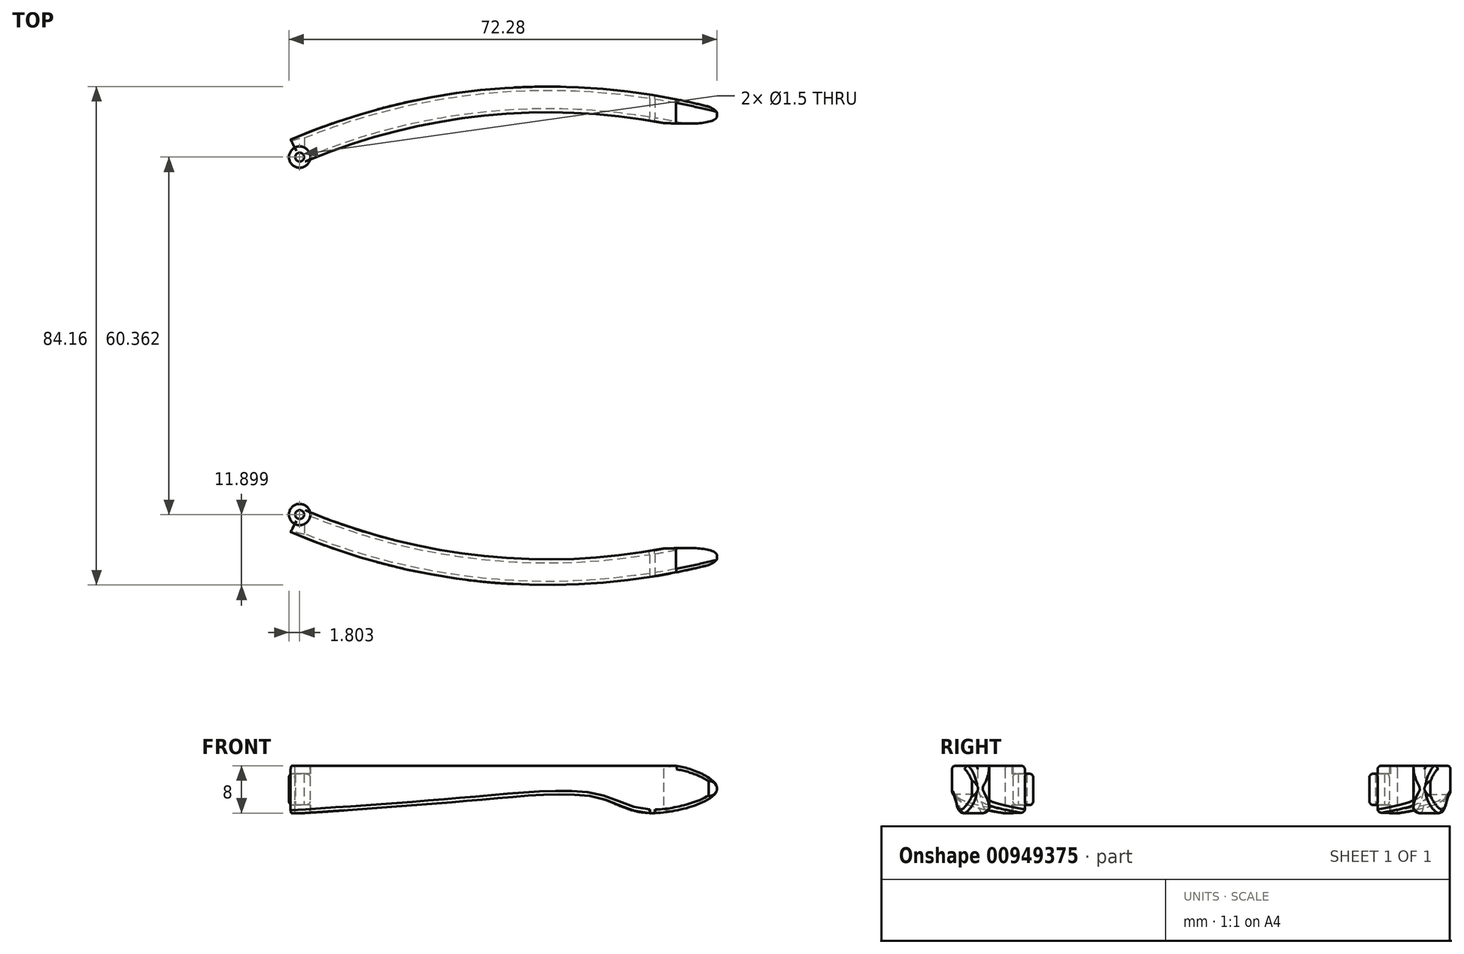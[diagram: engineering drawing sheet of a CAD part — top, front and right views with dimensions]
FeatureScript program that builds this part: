
annotation { "Feature Type Name" : "Feature", "Feature Type Description" : "" }
export const myFeature = defineFeature(function(context is Context, id is Id, definition is map)
    precondition{}
    {
        {
            var Q0;
            Q0=qCreatedBy(makeId("Top.planeOp"),FACE);
            var sketch = newSketch(context, id + "F0", { "sketchPlane" : qUnion([Q0])});
            skArc(sketch, "E0.0", {"start": v(25.58, 38.7) * mm, "mid": v(-10.17, 41.73) * mm, "end": v(-45, 33.11) * mm});
            skFitSpline(sketch, "E1", {"points": [v(25.58, 38.7) * mm, v(26.65, 36.57) * mm, v(17.96, 35.93) * mm], "startDerivative": vector(14.5, -5.54) * mm, "endDerivative": vector(-9.45, 0.25) * mm});
            skArc(sketch, "E2", {"start": v(17.96, 35.93) * mm, "mid": v(-13.01, 37.1) * mm, "end": v(-43, 29.25) * mm});
            skCircle(sketch, "E3", {"center": v(-43.48, 30.18) * mm, "radius": 0.75 * mm});
            skLineSegment(sketch, "E4", {"start": v(-45, 33.11) * mm, "end": v(-44.3, 31.78) * mm});
            skCircle(sketch, "E5.0", {"center": v(-43.48, 30.18) * mm, "radius": 1.8 * mm});
            skLineSegment(sketch, "E6", {"start": v(-44.3, 31.78) * mm, "end": v(-43, 29.25) * mm});
            skPoint(sketch, "E7", {"position": v(27, 36.94) * mm});
            skLineSegment(sketch, "E8", {"start": v(9.91, 0) * mm, "end": v(-97.59, 0) * mm, "construction": true});
            skLineSegment(sketch, "E9.MirrorCS", {"start": v(-45, -33.11) * mm, "end": v(-44.3, -31.78) * mm});
            skLineSegment(sketch, "E10.MirrorCS", {"start": v(-44.3, -31.78) * mm, "end": v(-43, -29.25) * mm});
            skCircle(sketch, "E11.MirrorC", {"center": v(-43.48, -30.18) * mm, "radius": 0.75 * mm});
            skFitSpline(sketch, "E12.MirrorCS", {"points": [v(25.58, -38.7) * mm, v(26.65, -36.57) * mm, v(17.96, -35.93) * mm], "startDerivative": vector(14.5, 5.54) * mm, "endDerivative": vector(-9.45, -0.25) * mm});
            skPoint(sketch, "E13.MirrorP", {"position": v(27, -36.94) * mm});
            skArc(sketch, "E14.MirrorCS", {"start": v(25.58, -38.7) * mm, "mid": v(-10.17, -41.73) * mm, "end": v(-45, -33.11) * mm});
            skCircle(sketch, "E15.MirrorC", {"center": v(-43.48, -30.18) * mm, "radius": 1.8 * mm});
            skArc(sketch, "E16.MirrorCS", {"start": v(17.96, -35.93) * mm, "mid": v(-13.01, -37.1) * mm, "end": v(-43, -29.25) * mm});
            skLineSegment(sketch, "E17", {"start": v(-45.08, 29.35) * mm, "end": v(-48.74, 36.44) * mm, "construction": true});
            skSolve(sketch);
        }
        {
            var Q0;
            Q0=makeQuery(id+"F0.imprint","IMPRINT",FACE,{"disambiguationData":[TD([[makeQuery(id+"F0.imprint","IMPRINT",EDGE,{"derivedFrom":sQuery(id+"F0.wireOp",EDGE,"E0.0")}),1.0]])]});
            var Q1;
            {var subQ2=sQuery(id+"F0.wireOp",EDGE,"E9.MirrorCS");Q1=makeQuery(id+"F0.imprint","IMPRINT",FACE,{"disambiguationData":[TD([[makeQuery(id+"F0.imprint","IMPRINT",EDGE,{"derivedFrom":subQ2}),-1.0]])]});}
            extrude(context, id + "F1", {"entities" : qUnion([Q0, Q1]), "endBound" : BoundingType.SYMMETRIC, "depth" : 8 * mm, "offsetDistance" : 25 * mm});
        }
        {
            var Q0;
            {var subQ1=sQuery(id+"F0.wireOp",EDGE,"E3");Q0=makeQuery(id+"F0.imprint","IMPRINT",FACE,{"disambiguationData":[TD([[makeQuery(id+"F0.imprint","IMPRINT",EDGE,{"derivedFrom":subQ1}),-1.0]])]});}
            var Q1;
            {var subQ0=sQuery(id+"F0.wireOp",EDGE,"E6");Q1=makeQuery(id+"F0.imprint","IMPRINT",FACE,{"disambiguationData":[TD([[makeQuery(id+"F0.imprint","IMPRINT",EDGE,{"derivedFrom":subQ0}),1.0]])]});}
            var Q2;
            {var subQ0=sQuery(id+"F0.wireOp",EDGE,"E10.MirrorCS");Q2=makeQuery(id+"F0.imprint","IMPRINT",FACE,{"disambiguationData":[TD([[makeQuery(id+"F0.imprint","IMPRINT",EDGE,{"derivedFrom":subQ0}),1.0]])]});}
            var Q3;
            {var subQ0=sQuery(id+"F0.wireOp",EDGE,"E10.MirrorCS");Q3=makeQuery(id+"F0.imprint","IMPRINT",FACE,{"disambiguationData":[TD([[makeQuery(id+"F0.imprint","IMPRINT",EDGE,{"derivedFrom":subQ0}),-1.0]])]});}
            extrude(context, id + "F2", {"entities" : qUnion([Q0, Q1, Q2, Q3]), "operationType" : NewBodyOperationType.ADD, "endBound" : BoundingType.SYMMETRIC, "depth" : 5.25 * mm, "offsetDistance" : 25 * mm});
        }
        {
            var Q0;
            Q0=qCreatedBy(makeId("Front.planeOp"),FACE);
            var sketch = newSketch(context, id + "F3", { "sketchPlane" : qUnion([Q0])});
            skFitSpline(sketch, "E18", {"points": [v(-45.83, -4.2) * mm, v(-13.3, -1.78) * mm, v(7.08, -1.45) * mm, v(15.62, -4) * mm, v(26.99, -0.04) * mm, v(19.86, 4.03) * mm], "startDerivative": vector(104.33, 6.52) * mm, "endDerivative": vector(-64.8, 9.1) * mm});
            skLineSegment(sketch, "E19", {"start": v(19.86, 4.03) * mm, "end": v(-45.83, 4.03) * mm});
            skLineSegment(sketch, "E20", {"start": v(-45.83, 4.03) * mm, "end": v(-45.83, -4.2) * mm});
            skLineSegment(sketch, "E21", {"start": v(19.86, 4.03) * mm, "end": v(23.93, 4.03) * mm});
            skLineSegment(sketch, "E22", {"start": v(32.74, -4.24) * mm, "end": v(-45.83, -4.2) * mm});
            skLineSegment(sketch, "E23", {"start": v(23.93, 4.03) * mm, "end": v(27.35, 4.03) * mm});
            skLineSegment(sketch, "E24", {"start": v(27.35, 4.03) * mm, "end": v(27.5, -4.11) * mm});
            skLineSegment(sketch, "E25", {"start": v(32.74, -4.24) * mm, "end": v(27.5, -4.11) * mm});
            skPoint(sketch, "E26", {"position": v(27.43, -0.04) * mm});
            skSolve(sketch);
        }
        {
            var Q0;
            {var subQ0=sQuery(id+"F3.wireOp",EDGE,"E22");Q0=makeQuery(id+"F3.imprint","IMPRINT",FACE,{"disambiguationData":[TD([[makeQuery(id+"F3.imprint","IMPRINT",EDGE,{"derivedFrom":subQ0}),-1.0]])]});}
            var Q1;
            {var subQ0=sQuery(id+"F3.wireOp",EDGE,"E21");Q1=makeQuery(id+"F3.imprint","IMPRINT",FACE,{"disambiguationData":[TD([[makeQuery(id+"F3.imprint","IMPRINT",EDGE,{"derivedFrom":subQ0}),-1.0]])]});}
            extrude(context, id + "F4", {"entities" : qUnion([Q0, Q1]), "operationType" : NewBodyOperationType.REMOVE, "endBound" : BoundingType.SYMMETRIC, "oppositeDirection" : true, "depth" : 250 * mm, "offsetDistance" : 25 * mm});
        }
        {
            var Q0;
            Q0=makeQuery(id+"F1.opExtrude","CAP_EDGE",EDGE,{"disambiguationData":[OSD([sQuery(id+"F0.wireOp",EDGE,"E0.0")])],"isStart":false});
            var Q1;
            Q1=makeQuery(id+"F4.boolean.opBoolean","INTERSECT",EDGE,{"disambiguationData":[OD(1.0)],"derivedFrom":[makeQuery(id+"F1.opExtrude","SWEPT_FACE",FACE,{"disambiguationData":[OSD([sQuery(id+"F0.wireOp",EDGE,"E0.0")])]}),makeQuery(id+"F4.opExtrude","SWEPT_FACE",FACE,{"disambiguationData":[OSD([sQuery(id+"F3.wireOp",EDGE,"E18")])]})]});
            var Q2;
            Q2=makeQuery(id+"F1.opExtrude","CAP_EDGE",EDGE,{"disambiguationData":[OSD([sQuery(id+"F0.wireOp",EDGE,"E2")])],"isStart":false});
            var Q3;
            Q3=makeQuery(id+"F4.boolean.opBoolean","INTERSECT",EDGE,{"disambiguationData":[OD(0.0)],"derivedFrom":[makeQuery(id+"F1.opExtrude","SWEPT_FACE",FACE,{"disambiguationData":[OSD([sQuery(id+"F0.wireOp",EDGE,"E2")])]}),makeQuery(id+"F4.opExtrude","SWEPT_FACE",FACE,{"disambiguationData":[OSD([sQuery(id+"F3.wireOp",EDGE,"E18")])]})]});
            var Q4;
            Q4=makeQuery(id+"F1.opExtrude","CAP_EDGE",EDGE,{"disambiguationData":[OSD([sQuery(id+"F0.wireOp",EDGE,"E16.MirrorCS")])],"isStart":false});
            var Q5;
            Q5=makeQuery(id+"F1.opExtrude","CAP_EDGE",EDGE,{"disambiguationData":[OSD([sQuery(id+"F0.wireOp",EDGE,"E14.MirrorCS")])],"isStart":false});
            var Q6;
            Q6=makeQuery(id+"F4.boolean.opBoolean","INTERSECT",EDGE,{"disambiguationData":[OD(1.0)],"derivedFrom":[makeQuery(id+"F1.opExtrude","SWEPT_FACE",FACE,{"disambiguationData":[OSD([sQuery(id+"F0.wireOp",EDGE,"E14.MirrorCS")])]}),makeQuery(id+"F4.opExtrude","SWEPT_FACE",FACE,{"disambiguationData":[OSD([sQuery(id+"F3.wireOp",EDGE,"E18")])]})]});
            var Q7;
            Q7=makeQuery(id+"F4.boolean.opBoolean","INTERSECT",EDGE,{"disambiguationData":[OD(0.0)],"derivedFrom":[makeQuery(id+"F1.opExtrude","SWEPT_FACE",FACE,{"disambiguationData":[OSD([sQuery(id+"F0.wireOp",EDGE,"E16.MirrorCS")])]}),makeQuery(id+"F4.opExtrude","SWEPT_FACE",FACE,{"disambiguationData":[OSD([sQuery(id+"F3.wireOp",EDGE,"E18")])]})]});
            fillet(context, id + "F5", {"entities" : qUnion([Q0, Q1, Q2, Q3, Q4, Q5, Q6, Q7]), "radius" : .6 * mm, "tangentPropagation" : true, "allowEdgeOverflow" : false});
        }
        {
            var Q0;
            {var subQ0=sQuery(id+"F0.wireOp",EDGE,"E5.0");Q0=makeQuery(id+"F2.boolean.opBoolean","SPLIT",EDGE,{"disambiguationData":[topologyDisambiguationEdgeConnected([makeQuery(id+"F2.opExtrude","SWEPT_FACE",FACE,{"disambiguationData":[OSD([subQ0])]})])],"derivedFrom":makeQuery(id+"F2.opExtrude","CAP_EDGE",EDGE,{"disambiguationData":[OSD([subQ0])],"isStart":false})});}
            var Q1;
            {var subQ0=sQuery(id+"F0.wireOp",EDGE,"E5.0");Q1=makeQuery(id+"F2.boolean.opBoolean","SPLIT",EDGE,{"disambiguationData":[topologyDisambiguationEdgeConnected([makeQuery(id+"F2.opExtrude","SWEPT_FACE",FACE,{"disambiguationData":[OSD([subQ0])]})])],"derivedFrom":makeQuery(id+"F2.opExtrude","CAP_EDGE",EDGE,{"disambiguationData":[OSD([subQ0])],"isStart":true})});}
            var Q2;
            {var subQ0=sQuery(id+"F0.wireOp",EDGE,"E15.MirrorC");Q2=makeQuery(id+"F2.boolean.opBoolean","SPLIT",EDGE,{"disambiguationData":[topologyDisambiguationEdgeConnected([makeQuery(id+"F2.opExtrude","SWEPT_FACE",FACE,{"disambiguationData":[OSD([subQ0])]})])],"derivedFrom":makeQuery(id+"F2.opExtrude","CAP_EDGE",EDGE,{"disambiguationData":[OSD([subQ0])],"isStart":false})});}
            var Q3;
            {var subQ0=sQuery(id+"F0.wireOp",EDGE,"E15.MirrorC");Q3=makeQuery(id+"F2.boolean.opBoolean","SPLIT",EDGE,{"disambiguationData":[topologyDisambiguationEdgeConnected([makeQuery(id+"F2.opExtrude","SWEPT_FACE",FACE,{"disambiguationData":[OSD([subQ0])]})])],"derivedFrom":makeQuery(id+"F2.opExtrude","CAP_EDGE",EDGE,{"disambiguationData":[OSD([subQ0])],"isStart":true})});}
            fillet(context, id + "F6", {"entities" : qUnion([Q0, Q1, Q2, Q3]), "radius" : .6 * mm, "tangentPropagation" : true, "allowEdgeOverflow" : false});
        }
    });
